# Revit family: JNRBH 6', 8' 12'
name_source: partatom
category: Mechanical Equipment
units: mm (PartAtom-declared; Revit-internal decimal feet)

## family parameters
Always vertical = Yes
Classification = None
Cut with Voids When Loaded = No
Part Type = Normal
Room Calculation Point = No
Round Connector Dimension = Use Diameter
Shared = No
Work Plane-Based = No

## types (7) — shared parameters
PAINTED METAL EXTERIOR = CHARCOAL BROWN
Product stops = TAG MOLDING COMPREHENSIVE : 1 1/4" TM
REFRIGERATION PIPING = COPPER PIPE

## per-type parameters (varying)
| type | CENTER LINE | Length | Number of Doors |
| 5 DOOR | 75" | 150" | MASTER DOOR : 30" X 68 3/8" 5 DOOR A SWING (LEFT OPENING) |
| 4 DOOR | 60" | 120" | MASTER DOOR : 30" X 68 3/8" 4 DOOR A SWING (LEFT OPENING) |
| 3 DOOR | 45" | 90" | MASTER DOOR : 30" X 68 3/8" 3 DOOR A SWING (LEFT OPENING) |
| 2 DOOR | 30" | 60" | MASTER DOOR : 30" X 68 3/8" 2 DOOR A SWING (LEFT OPENING) |
| 6' | 36" | 72" | MASTER DOOR : 6' |
| 8' | 48" | 96" | MASTER DOOR : 8' |
| 12' | 72" | 144" | MASTER DOOR : 12' |

## geometry (parser evidence)
native form markers: Blend x20, Sweep x32
no freeform markers — native parametric forms only
